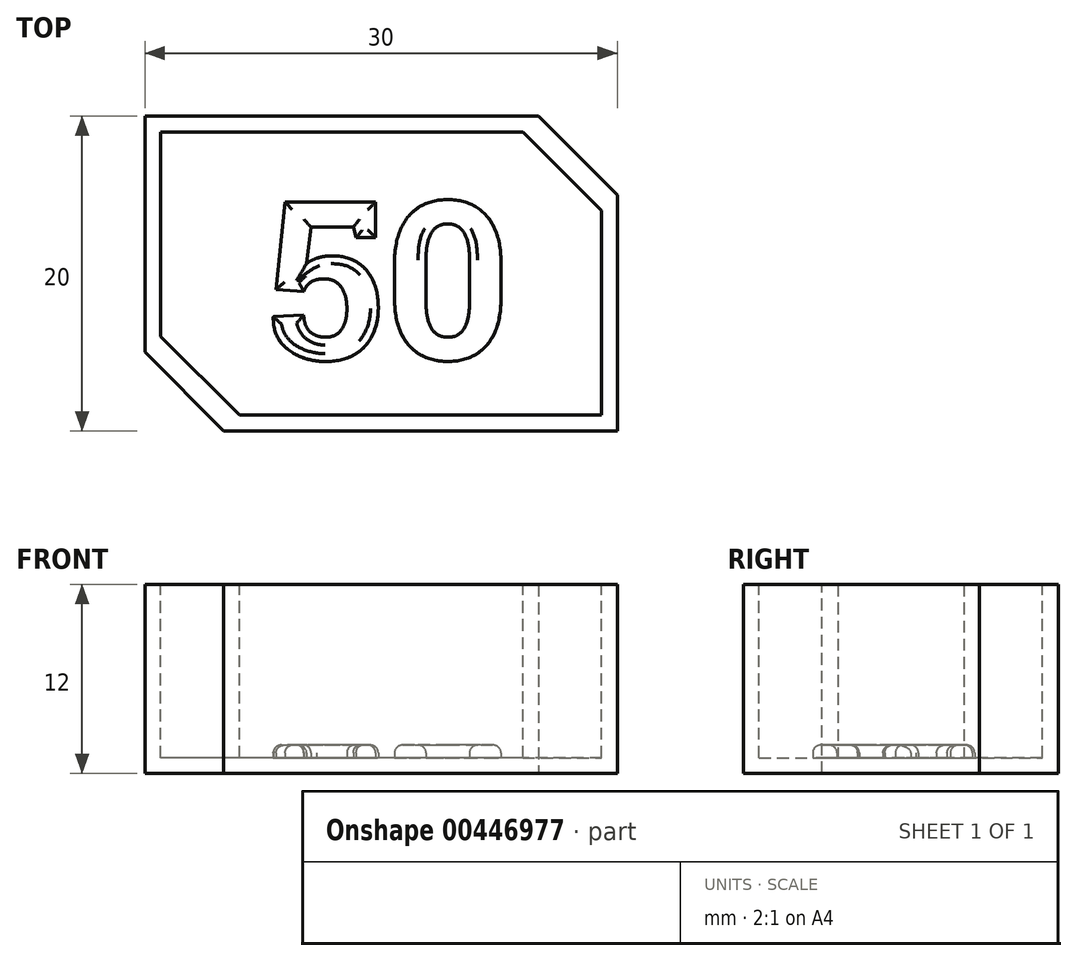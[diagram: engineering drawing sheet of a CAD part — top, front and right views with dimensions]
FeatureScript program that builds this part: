
annotation { "Feature Type Name" : "Feature", "Feature Type Description" : "" }
export const myFeature = defineFeature(function(context is Context, id is Id, definition is map)
    precondition{}
    {
        {
            var Q0;
            Q0=qCreatedBy(makeId("Top.planeOp"),FACE);
            var sketch = newSketch(context, id + "F0", { "sketchPlane" : qUnion([Q0])});
            skLineSegment(sketch, "E0.bottom", {"start": v(15, -10) * mm, "end": v(-15, -10) * mm});
            skLineSegment(sketch, "E0.top", {"start": v(15, 10) * mm, "end": v(-15, 10) * mm});
            skLineSegment(sketch, "E0.left", {"start": v(15, -10) * mm, "end": v(15, 10) * mm});
            skLineSegment(sketch, "E0.right", {"start": v(-15, -10) * mm, "end": v(-15, 10) * mm});
            skPoint(sketch, "E0.middle", {"position": v(0, 0) * mm});
            skSolve(sketch);
        }
        {
            var Q0;
            Q0 = qSketchRegion(id + "F0", true);
            extrude(context, id + "F1", {"entities" : qUnion([Q0]), "depth" : 12 * mm, "offsetDistance" : 25 * mm});
        }
        {
            var Q0;
            Q0=makeQuery(id+"F1.opExtrude","CAP_FACE",FACE,{"disambiguationData":[OSD([sQuery(id+"F0.wireOp",EDGE,"E0.bottom"),sQuery(id+"F0.wireOp",EDGE,"E0.top"),sQuery(id+"F0.wireOp",EDGE,"E0.left"),sQuery(id+"F0.wireOp",EDGE,"E0.right")])],"isStart":false});
            var sketch = newSketch(context, id + "F2", { "sketchPlane" : qUnion([Q0])});
            skLineSegment(sketch, "E1.bottom", {"start": v(14, -9) * mm, "end": v(-14, -9) * mm});
            skLineSegment(sketch, "E1.top", {"start": v(14, 9) * mm, "end": v(-14, 9) * mm});
            skLineSegment(sketch, "E1.left", {"start": v(14, -9) * mm, "end": v(14, 9) * mm});
            skLineSegment(sketch, "E1.right", {"start": v(-14, -9) * mm, "end": v(-14, 9) * mm});
            skPoint(sketch, "E1.middle", {"position": v(0, 0) * mm});
            skSolve(sketch);
        }
        {
            var Q0;
            Q0 = qSketchRegion(id + "F2", true);
            extrude(context, id + "F3", {"entities" : qUnion([Q0]), "operationType" : NewBodyOperationType.REMOVE, "oppositeDirection" : true, "depth" : 11 * mm, "offsetDistance" : 25 * mm});
        }
        {
            var Q0;
            Q0=makeQuery(id+"F3.boolean.opBoolean","COPY",EDGE,{"derivedFrom":makeQuery(id+"F3.opExtrude","SWEPT_EDGE",EDGE,{"disambiguationData":[OSD([sQuery(id+"F2.wireOp",EDGE,"E1.top"),sQuery(id+"F2.wireOp",EDGE,"E1.left")])]})});
            var Q1;
            Q1=makeQuery(id+"F3.boolean.opBoolean","COPY",EDGE,{"derivedFrom":makeQuery(id+"F3.opExtrude","SWEPT_EDGE",EDGE,{"disambiguationData":[OSD([sQuery(id+"F2.wireOp",EDGE,"E1.bottom"),sQuery(id+"F2.wireOp",EDGE,"E1.right")])]})});
            var Q2;
            Q2=makeQuery(id+"F1.opExtrude","SWEPT_EDGE",EDGE,{"disambiguationData":[OSD([sQuery(id+"F0.wireOp",EDGE,"E0.top"),sQuery(id+"F0.wireOp",EDGE,"E0.left")])]});
            var Q3;
            Q3=makeQuery(id+"F1.opExtrude","SWEPT_EDGE",EDGE,{"disambiguationData":[OSD([sQuery(id+"F0.wireOp",EDGE,"E0.bottom"),sQuery(id+"F0.wireOp",EDGE,"E0.right")])]});
            chamfer(context, id + "F4", {"entities" : qUnion([Q0, Q1, Q2, Q3]), "width" : 5 * mm, "tangentPropagation" : true});
        }
        {
            var Q0;
            Q0=makeQuery(id+"F3.boolean.opBoolean","COPY",FACE,{"derivedFrom":makeQuery(id+"F3.opExtrude","CAP_FACE",FACE,{"disambiguationData":[OSD([sQuery(id+"F2.wireOp",EDGE,"E1.bottom"),sQuery(id+"F2.wireOp",EDGE,"E1.top"),sQuery(id+"F2.wireOp",EDGE,"E1.left"),sQuery(id+"F2.wireOp",EDGE,"E1.right")])],"isStart":false})});
            var sketch = newSketch(context, id + "F5", { "sketchPlane" : qUnion([Q0])});
            skSolve(sketch);
        }
        {
            var Q0;
            {var subQ1=sQuery(id+"F2.wireOp",EDGE,"E1.top");Q0=makeQuery(id+"F5.imprint","IMPRINT",FACE,{"disambiguationData":[TD([[makeQuery(id+"F5.imprint","IMPRINT",EDGE,{"derivedFrom":makeQuery(id+"F3.boolean.opBoolean","COPY",EDGE,{"derivedFrom":makeQuery(id+"F3.opExtrude","CAP_EDGE",EDGE,{"disambiguationData":[OSD([subQ1])],"isStart":false})})}),1.0]])]});}
            var sketch = newSketch(context, id + "F6", { "sketchPlane" : qUnion([Q0])});
            skText(sketch, "E2", { "text": "50", "fontName": "RobotoSlab-Bold.ttf"});
            const initialGuessF6  = {"E2": [-0.00731, -0.00544, 1, 0, 0.01012]};
            skSetInitialGuess(sketch, initialGuessF6);
            skSolve(sketch);
        }
        {
            var Q0;
            Q0 = qSketchRegion(id + "F6", true);
            extrude(context, id + "F7", {"entities" : qUnion([Q0]), "operationType" : NewBodyOperationType.ADD, "depth" : 0.8 * mm, "offsetDistance" : 25 * mm});
        }
        {
            var Q0;
            Q0=makeQuery(id+"F7.opExtrude","CAP_EDGE",EDGE,{"disambiguationData":[OSD([sQuery(id+"F6.wireOp",EDGE,"E2.sketch_text.stroke-23")])],"isStart":false});
            var Q1;
            Q1=makeQuery(id+"F7.opExtrude","CAP_EDGE",EDGE,{"disambiguationData":[OSD([sQuery(id+"F6.wireOp",EDGE,"E2.sketch_text.stroke-22")])],"isStart":false});
            var Q2;
            Q2=makeQuery(id+"F7.opExtrude","CAP_EDGE",EDGE,{"disambiguationData":[OSD([sQuery(id+"F6.wireOp",EDGE,"E2.sketch_text.stroke-18")])],"isStart":false});
            var Q3;
            Q3=makeQuery(id+"F7.opExtrude","CAP_EDGE",EDGE,{"disambiguationData":[OSD([sQuery(id+"F6.wireOp",EDGE,"E2.sketch_text.stroke-24")])],"isStart":false});
            var Q4;
            Q4=makeQuery(id+"F7.opExtrude","CAP_EDGE",EDGE,{"disambiguationData":[OSD([sQuery(id+"F6.wireOp",EDGE,"E2.sketch_text.stroke-1")])],"isStart":false});
            var Q5;
            Q5=makeQuery(id+"F7.opExtrude","CAP_EDGE",EDGE,{"disambiguationData":[OSD([sQuery(id+"F6.wireOp",EDGE,"E2.sketch_text.stroke-25")])],"isStart":false});
            var Q6;
            Q6=makeQuery(id+"F7.opExtrude","CAP_EDGE",EDGE,{"disambiguationData":[OSD([sQuery(id+"F6.wireOp",EDGE,"E2.sketch_text.stroke-0")])],"isStart":false});
            var Q7;
            Q7=makeQuery(id+"F7.opExtrude","CAP_EDGE",EDGE,{"disambiguationData":[OSD([sQuery(id+"F6.wireOp",EDGE,"E2.sketch_text.stroke-2")])],"isStart":false});
            var Q8;
            Q8=makeQuery(id+"F7.opExtrude","CAP_EDGE",EDGE,{"disambiguationData":[OSD([sQuery(id+"F6.wireOp",EDGE,"E2.sketch_text.stroke-5")])],"isStart":false});
            var Q9;
            Q9=makeQuery(id+"F7.opExtrude","CAP_EDGE",EDGE,{"disambiguationData":[OSD([sQuery(id+"F6.wireOp",EDGE,"E2.sketch_text.stroke-4")])],"isStart":false});
            var Q10;
            Q10=makeQuery(id+"F7.opExtrude","CAP_EDGE",EDGE,{"disambiguationData":[OSD([sQuery(id+"F6.wireOp",EDGE,"E2.sketch_text.stroke-12")])],"isStart":false});
            var Q11;
            Q11=makeQuery(id+"F7.opExtrude","CAP_EDGE",EDGE,{"disambiguationData":[OSD([sQuery(id+"F6.wireOp",EDGE,"E2.sketch_text.stroke-21")])],"isStart":false});
            var Q12;
            Q12=makeQuery(id+"F7.opExtrude","CAP_EDGE",EDGE,{"disambiguationData":[OSD([sQuery(id+"F6.wireOp",EDGE,"E2.sketch_text.stroke-32")])],"isStart":false});
            var Q13;
            Q13=makeQuery(id+"F7.opExtrude","CAP_EDGE",EDGE,{"disambiguationData":[OSD([sQuery(id+"F6.wireOp",EDGE,"E2.sketch_text.stroke-38")])],"isStart":false});
            fillet(context, id + "F8", {"entities" : qUnion([Q0, Q1, Q2, Q3, Q4, Q5, Q6, Q7, Q8, Q9, Q10, Q11, Q12, Q13]), "radius" : 0.5 * mm, "tangentPropagation" : true, "allowEdgeOverflow" : false});
        }
    });
